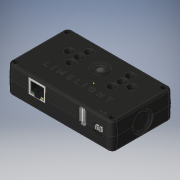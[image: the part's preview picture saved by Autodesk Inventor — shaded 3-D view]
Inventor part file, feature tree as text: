
AUTODESK INVENTOR PART (.ipt)
format: ipt  version: 2019 (Build 230136000, 136)  size: 4,892,160 bytes
history: native  units: in
note: dims shown in document units (in); Inventor stores cm internally (conversion verified against a paired STEP export)
features: other x11, sketch x1
ambient origin geometry x8: Origin, YZ Plane, XZ Plane, XY Plane, X Axis, Y Axis, Z Axis, Center Point
bodies: Solid2 (feature_tree), Solid3 (feature_tree), Solid4 (feature_tree), Solid5 (feature_tree), Solid6 (feature_tree), Solid7 (feature_tree), Solid8 (feature_tree), Solid9 (feature_tree), Solid10 (feature_tree), Solid11 (feature_tree), Solid12 (feature_tree), Solid13 (feature_tree), Solid1 (feature_tree)
feature tree (12):
  sketch  "Sketch1"
  other  "Solid2:1"
  other  "Solid3:1"
  other  "Solid4:1"
  other  "Solid5:1"
  other  "Solid6:1"
  other  "Solid7:1"
  other  "Solid8:1"
  other  "Solid9:1"
  other  "Solid10:1"
  other  "Solid11:1"
  other  "Solid12:1"
